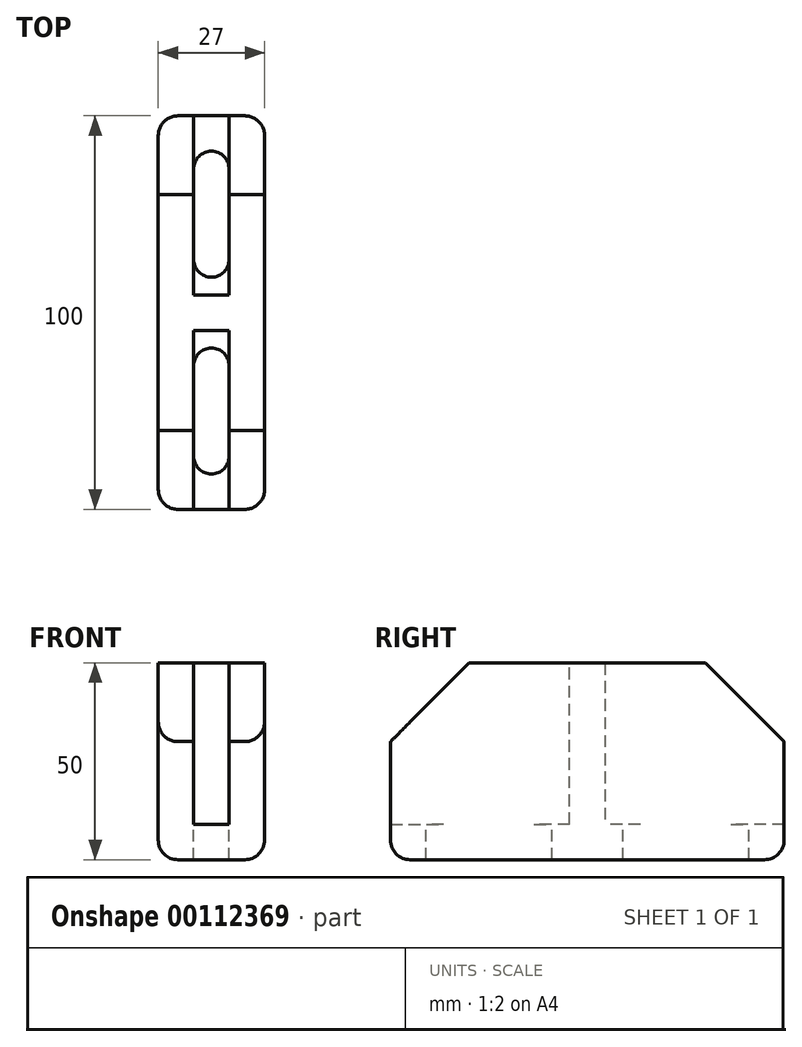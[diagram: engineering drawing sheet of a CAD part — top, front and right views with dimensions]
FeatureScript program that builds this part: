
annotation { "Feature Type Name" : "Feature", "Feature Type Description" : "" }
export const myFeature = defineFeature(function(context is Context, id is Id, definition is map)
    precondition{}
    {
        {
            var Q0;
            Q0=qCreatedBy(makeId("Top.planeOp"),FACE);
            var sketch = newSketch(context, id + "F0", { "sketchPlane" : qUnion([Q0])});
            skLineSegment(sketch, "E0", {"start": v(0, 0) * mm, "end": v(0, 50) * mm});
            skLineSegment(sketch, "E1", {"start": v(0, 50) * mm, "end": v(9, 50) * mm});
            skLineSegment(sketch, "E2", {"start": v(9, 50) * mm, "end": v(9, 4.5) * mm});
            skLineSegment(sketch, "E3", {"start": v(9, 4.5) * mm, "end": v(18, 4.5) * mm});
            skLineSegment(sketch, "E4", {"start": v(18, 4.5) * mm, "end": v(18, 50) * mm});
            skLineSegment(sketch, "E5", {"start": v(18, 50) * mm, "end": v(27, 50) * mm});
            skLineSegment(sketch, "E6", {"start": v(27, 50) * mm, "end": v(27, 22.5) * mm});
            skLineSegment(sketch, "E7", {"start": v(68, 13.5) * mm, "end": v(27, 13.5) * mm});
            skLineSegment(sketch, "E8", {"start": v(27, 13.5) * mm, "end": v(27, 4.5) * mm});
            skLineSegment(sketch, "E9", {"start": v(27, 4.5) * mm, "end": v(68, 4.5) * mm});
            skLineSegment(sketch, "E10", {"start": v(27, 0) * mm, "end": v(0, 0) * mm});
            skLineSegment(sketch, "E11", {"start": v(27, 4.5) * mm, "end": v(27, 0) * mm});
            skLineSegment(sketch, "E12", {"start": v(68, 4.5) * mm, "end": v(68, 13.5) * mm});
            skLineSegment(sketch, "E13", {"start": v(27, 22.5) * mm, "end": v(27, 13.5) * mm});
            skPoint(sketch, "E14.end.orphan", {"position": v(68, 0) * mm});
            skSolve(sketch);
        }
        {
            var Q0;
            Q0=qSketchRegion(id+"F0",true);
            extrude(context, id + "F1", {"entities" : qUnion([Q0]), "depth" : 41 * mm});
        }
        {
            var Q0;
            Q0=qCreatedBy(makeId("Top.planeOp"),FACE);
            var sketch = newSketch(context, id + "F2", { "sketchPlane" : qUnion([Q0])});
            skLineSegment(sketch, "E15", {"start": v(0, 0) * mm, "end": v(0, 50) * mm});
            skLineSegment(sketch, "E16", {"start": v(0, 50) * mm, "end": v(27, 50) * mm});
            skLineSegment(sketch, "E17", {"start": v(27, 50) * mm, "end": v(68, 13.5) * mm});
            skLineSegment(sketch, "E18", {"start": v(68, 13.5) * mm, "end": v(68, 0) * mm});
            skLineSegment(sketch, "E19", {"start": v(68, 0) * mm, "end": v(0, 0) * mm});
            skSolve(sketch);
        }
        {
            var Q0;
            Q0=qSketchRegion(id+"F2",true);
            extrude(context, id + "F3", {"entities" : qUnion([Q0]), "operationType" : NewBodyOperationType.ADD, "oppositeDirection" : true, "depth" : 9 * mm});
        }
        {
            var Q0;
            {var subQ0=sQuery(id+"F2.wireOp",EDGE,"E16");var subQ1=sQuery(id+"F2.wireOp",EDGE,"E17");var subQ2=sQuery(id+"F2.wireOp",EDGE,"E18");Q0=makeQuery(id+"F3.boolean.opBoolean","SPLIT",FACE,{"disambiguationData":[TD([makeQuery(id+"F1.opExtrude","SWEPT_FACE",FACE,{"disambiguationData":[OSD([sQuery(id+"F0.wireOp",EDGE,"E6")])]})])],"derivedFrom":makeQuery(id+"F3.opExtrude","CAP_FACE",FACE,{"disambiguationData":[OSD([sQuery(id+"F2.wireOp",EDGE,"E15"),subQ0,subQ1,subQ2,sQuery(id+"F2.wireOp",EDGE,"E19")])],"isStart":true})});}
            var sketch = newSketch(context, id + "F4", { "sketchPlane" : qUnion([Q0])});
            skLineSegment(sketch, "E20", {"start": v(31.5, 39.97) * mm, "end": v(56.18, 18) * mm});
            skLineSegment(sketch, "E21", {"start": v(56.18, 18) * mm, "end": v(31.5, 18) * mm});
            skLineSegment(sketch, "E22", {"start": v(31.5, 18) * mm, "end": v(31.5, 39.97) * mm});
            skSolve(sketch);
        }
        {
            var Q0;
            Q0=qSketchRegion(id+"F4",true);
            extrude(context, id + "F5", {"entities" : qUnion([Q0]), "operationType" : NewBodyOperationType.REMOVE, "endBound" : BoundingType.UP_TO_NEXT, "oppositeDirection" : true, "depth" : 25 * mm});
        }
        {
            var Q0;
            Q0=makeQuery(id+"F3.boolean.opBoolean","MERGE",FACE,{"derivedFrom":[makeQuery(id+"F1.opExtrude","SWEPT_FACE",FACE,{"disambiguationData":[OSD([sQuery(id+"F0.wireOp",EDGE,"E0")])]}),makeQuery(id+"F3.opExtrude","SWEPT_FACE",FACE,{"disambiguationData":[OSD([sQuery(id+"F2.wireOp",EDGE,"E15")])]})]});
            var sketch = newSketch(context, id + "F6", { "sketchPlane" : qUnion([Q0])});
            skLineSegment(sketch, "E23", {"start": v(-30, 41) * mm, "end": v(-50, 21) * mm});
            skLineSegment(sketch, "E24", {"start": v(-50, 21) * mm, "end": v(-50, 41) * mm});
            skLineSegment(sketch, "E25", {"start": v(-50, 41) * mm, "end": v(-30, 41) * mm});
            skSolve(sketch);
        }
        {
            var Q0;
            Q0=qSketchRegion(id+"F6",true);
            extrude(context, id + "F7", {"entities" : qUnion([Q0]), "operationType" : NewBodyOperationType.REMOVE, "oppositeDirection" : true, "depth" : 30 * mm});
        }
        {
            var Q0;
            Q0=makeQuery(id+"F3.boolean.opBoolean","MERGE",FACE,{"derivedFrom":[makeQuery(id+"F1.opExtrude","SWEPT_FACE",FACE,{"disambiguationData":[OSD([sQuery(id+"F0.wireOp",EDGE,"E10")])]}),makeQuery(id+"F3.opExtrude","SWEPT_FACE",FACE,{"disambiguationData":[OSD([sQuery(id+"F2.wireOp",EDGE,"E19")])]})]});
            var sketch = newSketch(context, id + "F8", { "sketchPlane" : qUnion([Q0])});
            skLineSegment(sketch, "E26", {"start": v(0, 41) * mm, "end": v(-20, 41) * mm});
            skLineSegment(sketch, "E27", {"start": v(-20, 41) * mm, "end": v(0, 21) * mm});
            skLineSegment(sketch, "E28", {"start": v(0, 21) * mm, "end": v(0, 41) * mm});
            skSolve(sketch);
        }
        {
            var Q0;
            Q0=qSketchRegion(id+"F8",true);
            extrude(context, id + "F9", {"entities" : qUnion([Q0]), "operationType" : NewBodyOperationType.REMOVE, "oppositeDirection" : true, "depth" : 30 * mm});
        }
        {
            var Q0;
            {var subQ0=sQuery(id+"F2.wireOp",EDGE,"E18");Q0=makeQuery(id+"F3.boolean.opBoolean","SPLIT",FACE,{"disambiguationData":[TD([makeQuery(id+"F1.opExtrude","SWEPT_FACE",FACE,{"disambiguationData":[OSD([sQuery(id+"F0.wireOp",EDGE,"E7")])]})])],"derivedFrom":makeQuery(id+"F3.opExtrude","CAP_FACE",FACE,{"disambiguationData":[OSD([sQuery(id+"F2.wireOp",EDGE,"E15"),sQuery(id+"F2.wireOp",EDGE,"E16"),sQuery(id+"F2.wireOp",EDGE,"E17"),subQ0,sQuery(id+"F2.wireOp",EDGE,"E19")])],"isStart":true})});}
            var sketch = newSketch(context, id + "F10", { "sketchPlane" : qUnion([Q0])});
            skLineSegment(sketch, "E29", {"start": v(59, 9) * mm, "end": v(59, 9) * mm});
            skLineSegment(sketch, "E30", {"start": v(27, 9) * mm, "end": v(27, 9) * mm});
            skLineSegment(sketch, "E31.bottom", {"start": v(13.5, 9) * mm, "end": v(13.5, 9) * mm});
            skLineSegment(sketch, "E31.top", {"start": v(13.5, 41) * mm, "end": v(13.5, 41) * mm});
            skLineSegment(sketch, "E31.left", {"start": v(9, 13.5) * mm, "end": v(9, 36.5) * mm});
            skLineSegment(sketch, "E31.right", {"start": v(18, 13.5) * mm, "end": v(18, 36.5) * mm});
            skPoint(sketch, "E32.visualSharp", {"position": v(9, 41) * mm});
            skArc(sketch, "E32.filletArc", {"start": v(13.5, 41) * mm, "mid": v(10.32, 39.68) * mm, "end": v(9, 36.5) * mm});
            skPoint(sketch, "E33.visualSharp", {"position": v(18, 41) * mm});
            skArc(sketch, "E33.filletArc", {"start": v(18, 36.5) * mm, "mid": v(16.68, 39.68) * mm, "end": v(13.5, 41) * mm});
            skPoint(sketch, "E34.visualSharp", {"position": v(18, 9) * mm});
            skArc(sketch, "E34.filletArc", {"start": v(13.5, 9) * mm, "mid": v(16.68, 10.32) * mm, "end": v(18, 13.5) * mm});
            skPoint(sketch, "E35.visualSharp", {"position": v(9, 9) * mm});
            skArc(sketch, "E35.filletArc", {"start": v(9, 13.5) * mm, "mid": v(10.32, 10.32) * mm, "end": v(13.5, 9) * mm});
            skPoint(sketch, "E36.visualSharp", {"position": v(59, 13.5) * mm});
            skPoint(sketch, "E37.visualSharp", {"position": v(27, 13.5) * mm});
            skPoint(sketch, "E38.visualSharp", {"position": v(27, 4.5) * mm});
            skLineSegment(sketch, "E39", {"start": v(59, 0) * mm, "end": v(59, 0) * mm});
            skLineSegment(sketch, "E40", {"start": v(54.5, 4.5) * mm, "end": v(40.5, 4.5) * mm});
            skLineSegment(sketch, "E41", {"start": v(36, 0) * mm, "end": v(36, 0) * mm});
            skLineSegment(sketch, "E42", {"start": v(36, 0) * mm, "end": v(59, 0) * mm});
            skPoint(sketch, "E43.visualSharp", {"position": v(36, 4.5) * mm});
            skArc(sketch, "E43.filletArc", {"start": v(40.5, 4.5) * mm, "mid": v(37.32, 3.18) * mm, "end": v(36, 0) * mm});
            skPoint(sketch, "E44.visualSharp", {"position": v(59, 4.5) * mm});
            skArc(sketch, "E44.filletArc", {"start": v(59, 0) * mm, "mid": v(57.68, 3.18) * mm, "end": v(54.5, 4.5) * mm});
            skSolve(sketch);
        }
        {
            var Q0;
            Q0=qSketchRegion(id+"F10",true);
            extrude(context, id + "F11", {"entities" : qUnion([Q0]), "operationType" : NewBodyOperationType.REMOVE, "endBound" : BoundingType.UP_TO_NEXT, "oppositeDirection" : true, "depth" : 25 * mm});
        }
        {
            var Q0;
            Q0=makeQuery(id+"F11.boolean.opBoolean","MERGE",FACE,{"derivedFrom":[makeQuery(id+"F1.opExtrude","SWEPT_FACE",FACE,{"disambiguationData":[OSD([sQuery(id+"F0.wireOp",EDGE,"E9")])]}),makeQuery(id+"F11.opExtrude","SWEPT_FACE",FACE,{"disambiguationData":[OSD([sQuery(id+"F10.wireOp",EDGE,"E40")])]})]});
            var sketch = newSketch(context, id + "F12", { "sketchPlane" : qUnion([Q0])});
            skLineSegment(sketch, "E45", {"start": v(68, 41) * mm, "end": v(48, 41) * mm});
            skLineSegment(sketch, "E46", {"start": v(48, 41) * mm, "end": v(68, 21) * mm});
            skLineSegment(sketch, "E47", {"start": v(68, 21) * mm, "end": v(68, 41) * mm});
            skLineSegment(sketch, "E48", {"start": v(44.27, 32) * mm, "end": v(59, 17.27) * mm});
            skLineSegment(sketch, "E49", {"start": v(59, 17.27) * mm, "end": v(59, 9) * mm});
            skLineSegment(sketch, "E50", {"start": v(59, 9) * mm, "end": v(36, 9) * mm});
            skLineSegment(sketch, "E51", {"start": v(36, 9) * mm, "end": v(36, 32) * mm});
            skLineSegment(sketch, "E52", {"start": v(36, 32) * mm, "end": v(44.27, 32) * mm});
            skSolve(sketch);
        }
        {
            var Q0;
            Q0=qSketchRegion(id+"F12",true);
            extrude(context, id + "F13", {"entities" : qUnion([Q0]), "operationType" : NewBodyOperationType.REMOVE, "oppositeDirection" : true, "depth" : 25 * mm});
        }
        {
            var Q0;
            Q0=makeQuery(id+"F5.boolean.opBoolean","COPY",EDGE,{"derivedFrom":makeQuery(id+"F5.opExtrude","SWEPT_EDGE",EDGE,{"disambiguationData":[OSD([sQuery(id+"F4.wireOp",EDGE,"E21"),sQuery(id+"F4.wireOp",EDGE,"E22")])]})});
            var Q1;
            Q1=makeQuery(id+"F5.boolean.opBoolean","COPY",EDGE,{"derivedFrom":makeQuery(id+"F5.opExtrude","SWEPT_EDGE",EDGE,{"disambiguationData":[OSD([sQuery(id+"F4.wireOp",EDGE,"E20"),sQuery(id+"F4.wireOp",EDGE,"E22")])]})});
            var Q2;
            Q2=makeQuery(id+"F5.boolean.opBoolean","COPY",EDGE,{"derivedFrom":makeQuery(id+"F5.opExtrude","SWEPT_EDGE",EDGE,{"disambiguationData":[OSD([sQuery(id+"F4.wireOp",EDGE,"E20"),sQuery(id+"F4.wireOp",EDGE,"E21")])]})});
            var Q3;
            Q3=makeQuery(id+"Fke6nAtu37N1twp_1.boolean.opBoolean","COPY",EDGE,{"derivedFrom":makeQuery(id+"Fke6nAtu37N1twp_1.opExtrude","SWEPT_EDGE",EDGE,{"disambiguationData":[OSD([sQuery(id+"FLkLUzk18Yqsw11_1.wireOp",EDGE,"UgqfIFqF-uCeZ-zkU2-vUuL-UTNmJ0hB5brx"),sQuery(id+"FLkLUzk18Yqsw11_1.wireOp",EDGE,"b1YdoGC3-3HXy-S0wB-CbvG-K9YkCtlA5N6y")])]})});
            var Q4;
            Q4=makeQuery(id+"Fke6nAtu37N1twp_1.boolean.opBoolean","COPY",EDGE,{"derivedFrom":makeQuery(id+"Fke6nAtu37N1twp_1.opExtrude","SWEPT_EDGE",EDGE,{"disambiguationData":[OSD([sQuery(id+"FLkLUzk18Yqsw11_1.wireOp",EDGE,"UgqfIFqF-uCeZ-zkU2-vUuL-UTNmJ0hB5brx"),sQuery(id+"FLkLUzk18Yqsw11_1.wireOp",EDGE,"mFuIhIl8-4tkZ-GOba-gkbD-4BMWQUx2QZ0Z")])]})});
            var Q5;
            Q5=makeQuery(id+"Fke6nAtu37N1twp_1.boolean.opBoolean","COPY",EDGE,{"derivedFrom":makeQuery(id+"Fke6nAtu37N1twp_1.opExtrude","SWEPT_EDGE",EDGE,{"disambiguationData":[OSD([sQuery(id+"FLkLUzk18Yqsw11_1.wireOp",EDGE,"b1YdoGC3-3HXy-S0wB-CbvG-K9YkCtlA5N6y"),sQuery(id+"FLkLUzk18Yqsw11_1.wireOp",EDGE,"9VS1dgw0-vnnE-xP6p-Edo7-gMmYFDxwRgyd")])]})});
            var Q6;
            Q6=makeQuery(id+"Fke6nAtu37N1twp_1.boolean.opBoolean","COPY",EDGE,{"derivedFrom":makeQuery(id+"Fke6nAtu37N1twp_1.opExtrude","SWEPT_EDGE",EDGE,{"disambiguationData":[OSD([sQuery(id+"FLkLUzk18Yqsw11_1.wireOp",EDGE,"9VS1dgw0-vnnE-xP6p-Edo7-gMmYFDxwRgyd"),sQuery(id+"FLkLUzk18Yqsw11_1.wireOp",EDGE,"mFuIhIl8-4tkZ-GOba-gkbD-4BMWQUx2QZ0Z")])]})});
            var Q7;
            Q7=makeQuery(id+"F13.boolean.opBoolean","COPY",EDGE,{"derivedFrom":makeQuery(id+"F13.opExtrude","SWEPT_EDGE",EDGE,{"disambiguationData":[OSD([sQuery(id+"F12.wireOp",EDGE,"E50"),sQuery(id+"F12.wireOp",EDGE,"E51")])]})});
            var Q8;
            Q8=makeQuery(id+"F13.boolean.opBoolean","COPY",EDGE,{"derivedFrom":makeQuery(id+"F13.opExtrude","SWEPT_EDGE",EDGE,{"disambiguationData":[OSD([sQuery(id+"F12.wireOp",EDGE,"E51"),sQuery(id+"F12.wireOp",EDGE,"E52")])]})});
            var Q9;
            Q9=makeQuery(id+"F13.boolean.opBoolean","COPY",EDGE,{"derivedFrom":makeQuery(id+"F13.opExtrude","SWEPT_EDGE",EDGE,{"disambiguationData":[OSD([sQuery(id+"F12.wireOp",EDGE,"E48"),sQuery(id+"F12.wireOp",EDGE,"E52")])]})});
            var Q10;
            Q10=makeQuery(id+"F13.boolean.opBoolean","COPY",EDGE,{"derivedFrom":makeQuery(id+"F13.opExtrude","SWEPT_EDGE",EDGE,{"disambiguationData":[OSD([sQuery(id+"F12.wireOp",EDGE,"E48"),sQuery(id+"F12.wireOp",EDGE,"E49")])]})});
            var Q11;
            Q11=makeQuery(id+"F13.boolean.opBoolean","COPY",EDGE,{"derivedFrom":makeQuery(id+"F13.opExtrude","SWEPT_EDGE",EDGE,{"disambiguationData":[OSD([sQuery(id+"F12.wireOp",EDGE,"E49"),sQuery(id+"F12.wireOp",EDGE,"E50")])]})});
            fillet(context, id + "F14", {"entities" : qUnion([Q0, Q1, Q2, Q3, Q4, Q5, Q6, Q7, Q8, Q9, Q10, Q11]), "radius" : 1 * mm, "tangentPropagation" : true, "allowEdgeOverflow" : false});
        }
        {
            var Q0;
            Q0=makeQuery(id+"F1.opExtrude","SWEPT_BODY",BODY,{"disambiguationData":[OSD([sQuery(id+"F0.wireOp",EDGE,"E0"),sQuery(id+"F0.wireOp",EDGE,"E1"),sQuery(id+"F0.wireOp",EDGE,"E2"),sQuery(id+"F0.wireOp",EDGE,"E3"),sQuery(id+"F0.wireOp",EDGE,"E4"),sQuery(id+"F0.wireOp",EDGE,"E5"),sQuery(id+"F0.wireOp",EDGE,"E6"),sQuery(id+"F0.wireOp",EDGE,"E7"),sQuery(id+"F0.wireOp",EDGE,"E9"),sQuery(id+"F0.wireOp",EDGE,"E10"),sQuery(id+"F0.wireOp",EDGE,"E11"),sQuery(id+"F0.wireOp",EDGE,"E12"),sQuery(id+"F0.wireOp",EDGE,"E13")])]});
            var Q1;
            {var subQ2=sQuery(id+"F0.wireOp",EDGE,"E10");var subQ3=sQuery(id+"F0.wireOp",EDGE,"E0");var subQ4=sQuery(id+"F2.wireOp",EDGE,"E19");Q1=makeQuery(id+"F11.boolean.opBoolean","SPLIT",FACE,{"disambiguationData":[TD([makeQuery(id+"F1.opExtrude","SWEPT_FACE",FACE,{"disambiguationData":[OSD([subQ3])]})])],"derivedFrom":makeQuery(id+"F3.boolean.opBoolean","MERGE",FACE,{"derivedFrom":[makeQuery(id+"F1.opExtrude","SWEPT_FACE",FACE,{"disambiguationData":[OSD([subQ2])]}),makeQuery(id+"F3.opExtrude","SWEPT_FACE",FACE,{"disambiguationData":[OSD([subQ4])]})]})});}
            mirror(context, id + "F15", {"operationType" : NewBodyOperationType.ADD, "entities" : qUnion([Q0]), "mirrorPlane" : qUnion([Q1])});
        }
        {
            var Q0;
            {var subQ0=makeQuery(id+"F1.opExtrude","CAP_FACE",FACE,{"disambiguationData":[OSD([sQuery(id+"F0.wireOp",EDGE,"E0"),sQuery(id+"F0.wireOp",EDGE,"E1"),sQuery(id+"F0.wireOp",EDGE,"E2"),sQuery(id+"F0.wireOp",EDGE,"E3"),sQuery(id+"F0.wireOp",EDGE,"E4"),sQuery(id+"F0.wireOp",EDGE,"E5"),sQuery(id+"F0.wireOp",EDGE,"E6"),sQuery(id+"F0.wireOp",EDGE,"E7"),sQuery(id+"F0.wireOp",EDGE,"E9"),sQuery(id+"F0.wireOp",EDGE,"E10"),sQuery(id+"F0.wireOp",EDGE,"E11"),sQuery(id+"F0.wireOp",EDGE,"E12"),sQuery(id+"F0.wireOp",EDGE,"E13")])],"isStart":false});Q0=makeQuery(id+"F15.boolean.opBoolean","MERGE",FACE,{"derivedFrom":[subQ0,makeQuery(id+"F15.opPattern","COPY",FACE,{"derivedFrom":subQ0,"instanceName":"1"})]});}
            var sketch = newSketch(context, id + "F16", { "sketchPlane" : qUnion([Q0])});
            skLineSegment(sketch, "E53", {"start": v(9, -4.5) * mm, "end": v(9, 4.5) * mm});
            skLineSegment(sketch, "E54", {"start": v(9, 4.5) * mm, "end": v(27, 4.5) * mm});
            skLineSegment(sketch, "E55", {"start": v(27, 4.5) * mm, "end": v(27, -4.5) * mm});
            skLineSegment(sketch, "E56", {"start": v(27, -4.5) * mm, "end": v(9, -4.5) * mm});
            skSolve(sketch);
        }
        {
            var Q0;
            Q0 = qSketchRegion(id + "F16", true);
            extrude(context, id + "F17", {"entities" : qUnion([Q0]), "operationType" : NewBodyOperationType.REMOVE, "oppositeDirection" : true, "depth" : 41 * mm});
        }
        {
            var Q0;
            {var subQ2=sQuery(id+"F0.wireOp",EDGE,"E4");var subQ4=sQuery(id+"F0.wireOp",EDGE,"E13");var subQ5=sQuery(id+"F0.wireOp",EDGE,"E6");var subQ6=sQuery(id+"F0.wireOp",EDGE,"E9");var subQ7=sQuery(id+"F0.wireOp",EDGE,"E7");var subQ8=makeQuery(id+"F1.opExtrude","CAP_FACE",FACE,{"disambiguationData":[OSD([sQuery(id+"F0.wireOp",EDGE,"E0"),sQuery(id+"F0.wireOp",EDGE,"E1"),sQuery(id+"F0.wireOp",EDGE,"E2"),sQuery(id+"F0.wireOp",EDGE,"E3"),subQ2,sQuery(id+"F0.wireOp",EDGE,"E5"),subQ5,subQ7,subQ6,sQuery(id+"F0.wireOp",EDGE,"E10"),sQuery(id+"F0.wireOp",EDGE,"E11"),sQuery(id+"F0.wireOp",EDGE,"E12"),subQ4])],"isStart":false});Q0=makeQuery(id+"F17.boolean.opBoolean","SPLIT",FACE,{"disambiguationData":[TD([makeQuery(id+"F15.opPattern","COPY",FACE,{"derivedFrom":makeQuery(id+"F7.boolean.opBoolean","COPY",FACE,{"disambiguationData":[OD(1.0)],"derivedFrom":makeQuery(id+"F7.opExtrude","SWEPT_FACE",FACE,{"disambiguationData":[OSD([sQuery(id+"F6.wireOp",EDGE,"E23")])]})}),"instanceName":"1"})])],"derivedFrom":makeQuery(id+"F15.boolean.opBoolean","MERGE",FACE,{"derivedFrom":[subQ8,makeQuery(id+"F15.opPattern","COPY",FACE,{"derivedFrom":subQ8,"instanceName":"1"})]})});}
            var sketch = newSketch(context, id + "F18", { "sketchPlane" : qUnion([Q0])});
            skLineSegment(sketch, "E57", {"start": v(27, -13.5) * mm, "end": v(27, -65.43) * mm});
            skLineSegment(sketch, "E58", {"start": v(27, -65.43) * mm, "end": v(95.07, -18.05) * mm});
            skLineSegment(sketch, "E59", {"start": v(95.07, -18.05) * mm, "end": v(92.96, 35.74) * mm});
            skLineSegment(sketch, "E60", {"start": v(92.96, 35.74) * mm, "end": v(27, 70.5) * mm});
            skLineSegment(sketch, "E61", {"start": v(27, 70.5) * mm, "end": v(27, -13.5) * mm});
            skSolve(sketch);
        }
        {
            var Q0;
            Q0 = qSketchRegion(id + "F18", true);
            extrude(context, id + "F19", {"entities" : qUnion([Q0]), "operationType" : NewBodyOperationType.REMOVE, "endBound" : BoundingType.THROUGH_ALL, "oppositeDirection" : true, "depth" : 25 * mm});
        }
        {
            var Q0;
            Q0=makeQuery(id+"F19.boolean.opBoolean","MERGE",EDGE,{"derivedFrom":[makeQuery(id+"F15.opPattern","COPY",EDGE,{"derivedFrom":makeQuery(id+"F3.opExtrude","SWEPT_EDGE",EDGE,{"disambiguationData":[OSD([sQuery(id+"F2.wireOp",EDGE,"E16"),sQuery(id+"F2.wireOp",EDGE,"E17")])]}),"instanceName":"1"}),makeQuery(id+"F15.opPattern","COPY",EDGE,{"derivedFrom":makeQuery(id+"F1.opExtrude","SWEPT_EDGE",EDGE,{"disambiguationData":[OSD([sQuery(id+"F0.wireOp",EDGE,"E5"),sQuery(id+"F0.wireOp",EDGE,"E6")])]}),"instanceName":"1"})]});
            var Q1;
            Q1=makeQuery(id+"F15.opPattern","COPY",EDGE,{"derivedFrom":makeQuery(id+"F3.boolean.opBoolean","MERGE",EDGE,{"derivedFrom":[makeQuery(id+"F1.opExtrude","SWEPT_EDGE",EDGE,{"disambiguationData":[OSD([sQuery(id+"F0.wireOp",EDGE,"E0"),sQuery(id+"F0.wireOp",EDGE,"E1")])]}),makeQuery(id+"F3.opExtrude","SWEPT_EDGE",EDGE,{"disambiguationData":[OSD([sQuery(id+"F2.wireOp",EDGE,"E15"),sQuery(id+"F2.wireOp",EDGE,"E16")])]})]}),"instanceName":"1"});
            var Q2;
            Q2=makeQuery(id+"F19.boolean.opBoolean","MERGE",EDGE,{"derivedFrom":[makeQuery(id+"F3.opExtrude","SWEPT_EDGE",EDGE,{"disambiguationData":[OSD([sQuery(id+"F2.wireOp",EDGE,"E16"),sQuery(id+"F2.wireOp",EDGE,"E17")])]}),makeQuery(id+"F1.opExtrude","SWEPT_EDGE",EDGE,{"disambiguationData":[OSD([sQuery(id+"F0.wireOp",EDGE,"E5"),sQuery(id+"F0.wireOp",EDGE,"E6")])]})]});
            var Q3;
            Q3=makeQuery(id+"F3.boolean.opBoolean","MERGE",EDGE,{"derivedFrom":[makeQuery(id+"F1.opExtrude","SWEPT_EDGE",EDGE,{"disambiguationData":[OSD([sQuery(id+"F0.wireOp",EDGE,"E0"),sQuery(id+"F0.wireOp",EDGE,"E1")])]}),makeQuery(id+"F3.opExtrude","SWEPT_EDGE",EDGE,{"disambiguationData":[OSD([sQuery(id+"F2.wireOp",EDGE,"E15"),sQuery(id+"F2.wireOp",EDGE,"E16")])]})]});
            var Q4;
            {var subQ0=makeQuery(id+"F3.opExtrude","CAP_EDGE",EDGE,{"disambiguationData":[OSD([sQuery(id+"F2.wireOp",EDGE,"E15")])],"isStart":false});Q4=makeQuery(id+"F15.boolean.opBoolean","MERGE",EDGE,{"derivedFrom":[subQ0,makeQuery(id+"F15.opPattern","COPY",EDGE,{"derivedFrom":subQ0,"instanceName":"1"})]});}
            var Q5;
            {var subQ0=makeQuery(id+"F3.opExtrude","CAP_FACE",FACE,{"disambiguationData":[OSD([sQuery(id+"F2.wireOp",EDGE,"E15"),sQuery(id+"F2.wireOp",EDGE,"E16"),sQuery(id+"F2.wireOp",EDGE,"E17"),sQuery(id+"F2.wireOp",EDGE,"E18"),sQuery(id+"F2.wireOp",EDGE,"E19")])],"isStart":false});Q5=makeQuery(id+"F19.boolean.opBoolean","INTERSECT",EDGE,{"derivedFrom":[makeQuery(id+"F15.boolean.opBoolean","MERGE",FACE,{"derivedFrom":[subQ0,makeQuery(id+"F15.opPattern","COPY",FACE,{"derivedFrom":subQ0,"instanceName":"1"})]}),makeQuery(id+"F19.opExtrude","SWEPT_FACE",FACE,{"disambiguationData":[OSD([sQuery(id+"F18.wireOp",EDGE,"E57"),sQuery(id+"F18.wireOp",EDGE,"E61")])]})]});}
            var Q6;
            Q6=makeQuery(id+"F3.opExtrude","CAP_EDGE",EDGE,{"disambiguationData":[OSD([sQuery(id+"F2.wireOp",EDGE,"E16")])],"isStart":false});
            var Q7;
            Q7=makeQuery(id+"F15.opPattern","COPY",EDGE,{"derivedFrom":makeQuery(id+"F3.opExtrude","CAP_EDGE",EDGE,{"disambiguationData":[OSD([sQuery(id+"F2.wireOp",EDGE,"E16")])],"isStart":false}),"instanceName":"1"});
            fillet(context, id + "F20", {"entities" : qUnion([Q0, Q1, Q2, Q3, Q4, Q5, Q6, Q7]), "radius" : 5 * mm, "tangentPropagation" : true, "allowEdgeOverflow" : false});
        }
        {
            var Q0;
            {var subQ0=makeQuery(id+"F1.opExtrude","SWEPT_FACE",FACE,{"disambiguationData":[OSD([sQuery(id+"F0.wireOp",EDGE,"E6"),sQuery(id+"F0.wireOp",EDGE,"E13")])]});Q0=makeQuery(id+"F19.boolean.opBoolean","MERGE",FACE,{"derivedFrom":[subQ0,makeQuery(id+"F15.opPattern","COPY",FACE,{"derivedFrom":subQ0,"instanceName":"1"}),makeQuery(id+"F19.opExtrude","SWEPT_FACE",FACE,{"disambiguationData":[OSD([sQuery(id+"F18.wireOp",EDGE,"E57"),sQuery(id+"F18.wireOp",EDGE,"E61")])]})]});}
            var sketch = newSketch(context, id + "F21", { "sketchPlane" : qUnion([Q0])});
            skLineSegment(sketch, "E62.bottom", {"start": v(-4.5, 41) * mm, "end": v(4.5, 41) * mm});
            skLineSegment(sketch, "E62.top", {"start": v(-4.5, 0) * mm, "end": v(4.5, 0) * mm});
            skLineSegment(sketch, "E62.left", {"start": v(-4.5, 41) * mm, "end": v(-4.5, 0) * mm});
            skLineSegment(sketch, "E62.right", {"start": v(4.5, 41) * mm, "end": v(4.5, 0) * mm});
            skSolve(sketch);
        }
        {
            var Q0;
            Q0 = qSketchRegion(id + "F21", true);
            extrude(context, id + "F22", {"entities" : qUnion([Q0]), "operationType" : NewBodyOperationType.REMOVE, "oppositeDirection" : true, "depth" : 30 * mm});
        }
        {
            var Q0;
            {var subQ0=sQuery(id+"F2.wireOp",EDGE,"E19");var subQ2=makeQuery(id+"F1.opExtrude","SWEPT_FACE",FACE,{"disambiguationData":[OSD([sQuery(id+"F0.wireOp",EDGE,"E11")])]});var subQ4=makeQuery(id+"F1.opExtrude","SWEPT_FACE",FACE,{"disambiguationData":[OSD([sQuery(id+"F0.wireOp",EDGE,"E9")])]});var subQ5=sQuery(id+"F2.wireOp",EDGE,"E18");var subQ6=sQuery(id+"F2.wireOp",EDGE,"E16");var subQ7=makeQuery(id+"F3.opExtrude","CAP_FACE",FACE,{"disambiguationData":[OSD([sQuery(id+"F2.wireOp",EDGE,"E15"),subQ6,sQuery(id+"F2.wireOp",EDGE,"E17"),subQ5,subQ0])],"isStart":true});var subQ8=makeQuery(id+"F11.boolean.opBoolean","SPLIT",FACE,{"disambiguationData":[TD([subQ2])],"derivedFrom":makeQuery(id+"F3.boolean.opBoolean","SPLIT",FACE,{"disambiguationData":[TD([subQ4])],"derivedFrom":subQ7})});var subQ10=makeQuery(id+"F1.opExtrude","SWEPT_FACE",FACE,{"disambiguationData":[OSD([sQuery(id+"F0.wireOp",EDGE,"E3")])]});var subQ11=makeQuery(id+"F1.opExtrude","SWEPT_FACE",FACE,{"disambiguationData":[OSD([sQuery(id+"F0.wireOp",EDGE,"E2")])]});var subQ12=makeQuery(id+"F11.boolean.opBoolean","SPLIT",FACE,{"disambiguationData":[TD([subQ10])],"derivedFrom":makeQuery(id+"F3.boolean.opBoolean","SPLIT",FACE,{"disambiguationData":[TD([subQ11])],"derivedFrom":subQ7})});Q0=makeQuery(id+"F22.boolean.opBoolean","MERGE",FACE,{"derivedFrom":[makeQuery(id+"F17.boolean.opBoolean","MERGE",FACE,{"derivedFrom":[subQ12,makeQuery(id+"F15.opPattern","COPY",FACE,{"derivedFrom":subQ12,"instanceName":"1"}),makeQuery(id+"F15.boolean.opBoolean","MERGE",FACE,{"derivedFrom":[subQ8,makeQuery(id+"F15.opPattern","COPY",FACE,{"derivedFrom":subQ8,"instanceName":"1"})]}),makeQuery(id+"F17.opExtrude","CAP_FACE",FACE,{"disambiguationData":[OSD([sQuery(id+"F16.wireOp",EDGE,"E53"),sQuery(id+"F16.wireOp",EDGE,"E54"),sQuery(id+"F16.wireOp",EDGE,"E55"),sQuery(id+"F16.wireOp",EDGE,"E56")])],"isStart":false})]}),makeQuery(id+"F22.opExtrude","SWEPT_FACE",FACE,{"disambiguationData":[OSD([sQuery(id+"F21.wireOp",EDGE,"E62.top")])]})]});}
            var sketch = newSketch(context, id + "F23", { "sketchPlane" : qUnion([Q0])});
            skLineSegment(sketch, "E63.bottom", {"start": v(0, 4.5) * mm, "end": v(27, 4.5) * mm});
            skLineSegment(sketch, "E63.top", {"start": v(0, -4.5) * mm, "end": v(27, -4.5) * mm});
            skLineSegment(sketch, "E63.left", {"start": v(0, 4.5) * mm, "end": v(0, -4.5) * mm});
            skLineSegment(sketch, "E63.right", {"start": v(27, 4.5) * mm, "end": v(27, -4.5) * mm});
            skSolve(sketch);
        }
        {
            var Q0;
            Q0 = qSketchRegion(id + "F23", true);
            extrude(context, id + "F24", {"entities" : qUnion([Q0]), "operationType" : NewBodyOperationType.ADD, "depth" : 41 * mm});
        }
    });
